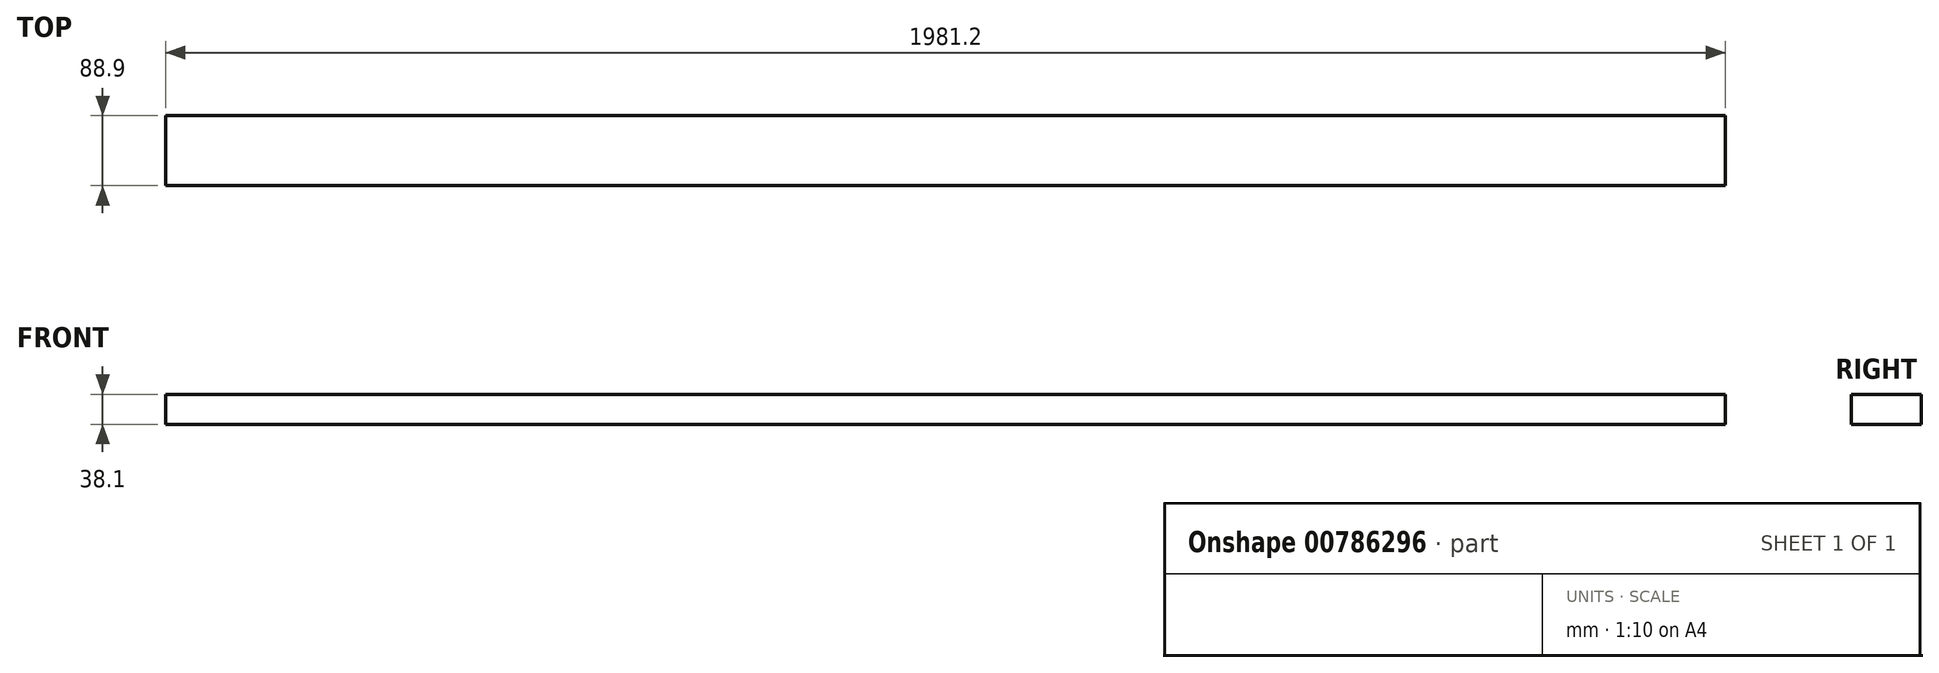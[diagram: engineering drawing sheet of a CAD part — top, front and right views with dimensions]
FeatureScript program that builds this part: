
annotation { "Feature Type Name" : "Feature", "Feature Type Description" : "" }
export const myFeature = defineFeature(function(context is Context, id is Id, definition is map)
    precondition{}
    {
        {
            var Q0;
            Q0=qCreatedBy(makeId("Front.planeOp"),FACE);
            var sketch = newSketch(context, id + "F0", { "sketchPlane" : qUnion([Q0])});
            skLineSegment(sketch, "E0.bottom", {"start": v(-990.6, 19.05) * mm, "end": v(990.6, 19.05) * mm});
            skLineSegment(sketch, "E0.top", {"start": v(-990.6, -19.05) * mm, "end": v(990.6, -19.05) * mm});
            skLineSegment(sketch, "E0.left", {"start": v(-990.6, 19.05) * mm, "end": v(-990.6, -19.05) * mm});
            skLineSegment(sketch, "E0.right", {"start": v(990.6, 19.05) * mm, "end": v(990.6, -19.05) * mm});
            skPoint(sketch, "E0.middle", {"position": v(0, 0) * mm});
            skSolve(sketch);
        }
        {
            var Q0;
            Q0=makeQuery(id+"F0.imprint","IMPRINT",FACE,{"disambiguationData":[TD([[makeQuery(id+"F0.imprint","IMPRINT",EDGE,{"derivedFrom":sQuery(id+"F0.wireOp",EDGE,"E0.bottom")}),-1.0]])]});
            extrude(context, id + "F1", {"entities" : qUnion([Q0]), "endBound" : BoundingType.SYMMETRIC, "depth" : 88.9 * mm, "offsetDistance" : 25.4 * mm});
        }
    });
